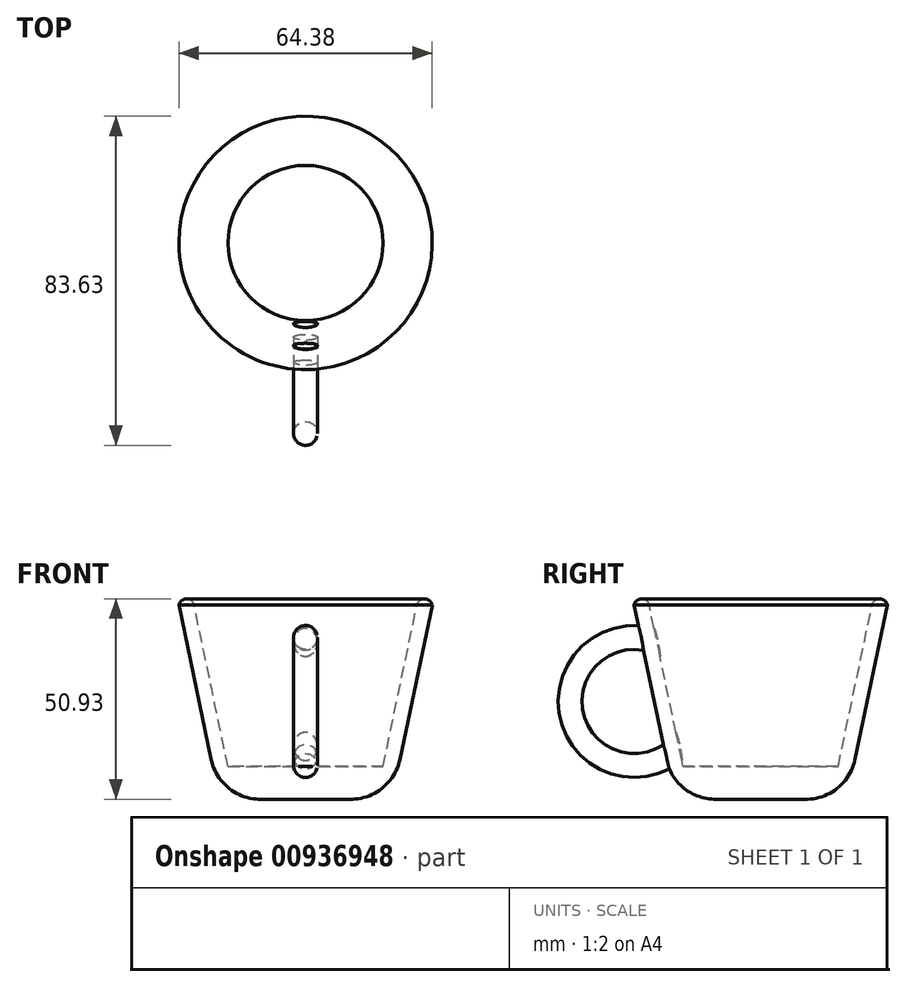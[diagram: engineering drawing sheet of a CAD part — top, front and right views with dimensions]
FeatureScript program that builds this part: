
annotation { "Feature Type Name" : "Feature", "Feature Type Description" : "" }
export const myFeature = defineFeature(function(context is Context, id is Id, definition is map)
    precondition{}
    {
        {
            var Q0;
            Q0=qCreatedBy(makeId("Front.planeOp"),FACE);
            var sketch = newSketch(context, id + "F0", { "sketchPlane" : qUnion([Q0])});
            skLineSegment(sketch, "E0", {"start": v(0, 0) * mm, "end": v(22.8, 0) * mm});
            skLineSegment(sketch, "E1", {"start": v(22.8, 0) * mm, "end": v(32.2, 44.83) * mm});
            skLineSegment(sketch, "E2.0", {"start": v(19.7, 3.8) * mm, "end": v(28.3, 44.83) * mm});
            skLineSegment(sketch, "E2.1", {"start": v(0, 3.8) * mm, "end": v(19.7, 3.81) * mm});
            skArc(sketch, "E3", {"start": v(28.3, 44.83) * mm, "mid": v(30.25, 46.4) * mm, "end": v(32.2, 44.83) * mm});
            skFitSpline(sketch, "E4", {"points": [v(22.8, 0) * mm, v(18.6, -2.99) * mm, v(0, -4.4) * mm], "startDerivative": vector(-13.97, -10.41) * mm, "endDerivative": vector(-71.95, 1.53) * mm});
            skLineSegment(sketch, "E5", {"start": v(0, 3.8) * mm, "end": v(0, -4.4) * mm});
            skSolve(sketch);
        }
        {
            var Q0;
            Q0=qCreatedBy(makeId("Front.planeOp"),FACE);
            var sketch = newSketch(context, id + "F1", { "sketchPlane" : qUnion([Q0])});
            skLineSegment(sketch, "E6", {"start": v(0, -7.05) * mm, "end": v(0, 60.23) * mm, "construction": true});
            skSolve(sketch);
        }
        {
            var Q0;
            Q0 = qSketchRegion(id + "F0", true);
            var Q1;
            Q1=sQuery(id+"F1.wireOp",EDGE,"E6");
            revolve(context, id + "F2", {"surfaceOperationType" : NewSurfaceOperationType.NEW, "entities" : qUnion([Q0]), "axis" : qUnion([Q1]), "revolveType" : RevolveType.FULL});
        }
        {
            var Q0;
            Q0=qCreatedBy(makeId("Front.planeOp"),FACE);
            cPlane(context, id + "F3", {"entities" : qUnion([Q0]), "cplaneType" : CPlaneType.OFFSET, "offset" : 32.14 * mm, "width" : 152.4 * mm, "height" : 152.4 * mm});
        }
        {
            var Q0;
            Q0=qCreatedBy(id+"F3.planeOp",FACE);
            var sketch = newSketch(context, id + "F4", { "sketchPlane" : qUnion([Q0])});
            skCircle(sketch, "E7", {"center": v(0, 36.6) * mm, "radius": 3.03 * mm});
            skSolve(sketch);
        }
        {
            var Q0;
            Q0=qCreatedBy(id+"F3.planeOp",FACE);
            var sketch = newSketch(context, id + "F5", { "sketchPlane" : qUnion([Q0])});
            skLineSegment(sketch, "E8", {"start": v(13.04, 20.34) * mm, "end": v(-13.93, 20.34) * mm, "construction": true});
            skSolve(sketch);
        }
        {
            var Q0;
            Q0=makeQuery(id+"F4.imprint","IMPRINT",FACE,{"disambiguationData":[TD([[makeQuery(id+"F4.imprint","IMPRINT",EDGE,{"derivedFrom":sQuery(id+"F4.wireOp",EDGE,"E7")}),1.0]])]});
            var Q1;
            Q1=sQuery(id+"F5.wireOp",EDGE,"E8");
            revolve(context, id + "F6", {"operationType" : NewBodyOperationType.ADD, "surfaceOperationType" : NewSurfaceOperationType.NEW, "entities" : qUnion([Q0]), "axis" : qUnion([Q1]), "revolveType" : RevolveType.FULL});
        }
        {
            var Q0;
            Q0=qCreatedBy(makeId("Front.planeOp"),FACE);
            var sketch = newSketch(context, id + "F7", { "sketchPlane" : qUnion([Q0])});
            skLineSegment(sketch, "E9", {"start": v(0, 3.86) * mm, "end": v(19.67, 3.86) * mm});
            skLineSegment(sketch, "E10", {"start": v(19.67, 3.86) * mm, "end": v(29.07, 48.9) * mm});
            skLineSegment(sketch, "E11", {"start": v(29.07, 48.9) * mm, "end": v(0, 48.9) * mm});
            skLineSegment(sketch, "E12", {"start": v(0, 48.9) * mm, "end": v(0, 3.86) * mm});
            skSolve(sketch);
        }
        {
            var Q0;
            Q0=qCreatedBy(makeId("Front.planeOp"),FACE);
            var sketch = newSketch(context, id + "F8", { "sketchPlane" : qUnion([Q0])});
            skLineSegment(sketch, "E13", {"start": v(0, -6.15) * mm, "end": v(0, 57.1) * mm, "construction": true});
            skSolve(sketch);
        }
        {
            var Q0;
            Q0=makeQuery(id+"F7.imprint","IMPRINT",FACE,{"disambiguationData":[TD([[makeQuery(id+"F7.imprint","IMPRINT",EDGE,{"derivedFrom":sQuery(id+"F7.wireOp",EDGE,"E9")}),1.0]])]});
            var Q1;
            Q1=sQuery(id+"F8.wireOp",EDGE,"E13");
            revolve(context, id + "F9", {"operationType" : NewBodyOperationType.REMOVE, "surfaceOperationType" : NewSurfaceOperationType.NEW, "entities" : qUnion([Q0]), "axis" : qUnion([Q1]), "revolveType" : RevolveType.FULL, "oppositeDirection" : true});
        }
        {
            var Q0;
            Q0=makeQuery(id+"F2.opRevolve","SWEPT_EDGE",EDGE,{"disambiguationData":[OSD([sQuery(id+"F0.wireOp",EDGE,"E0"),sQuery(id+"F0.wireOp",EDGE,"E1"),sQuery(id+"F0.wireOp",EDGE,"E4")])]});
            fillet(context, id + "F10", {"entities" : qUnion([Q0]), "radius" : 12.7 * mm, "tangentPropagation" : true, "allowEdgeOverflow" : false});
        }
    });
